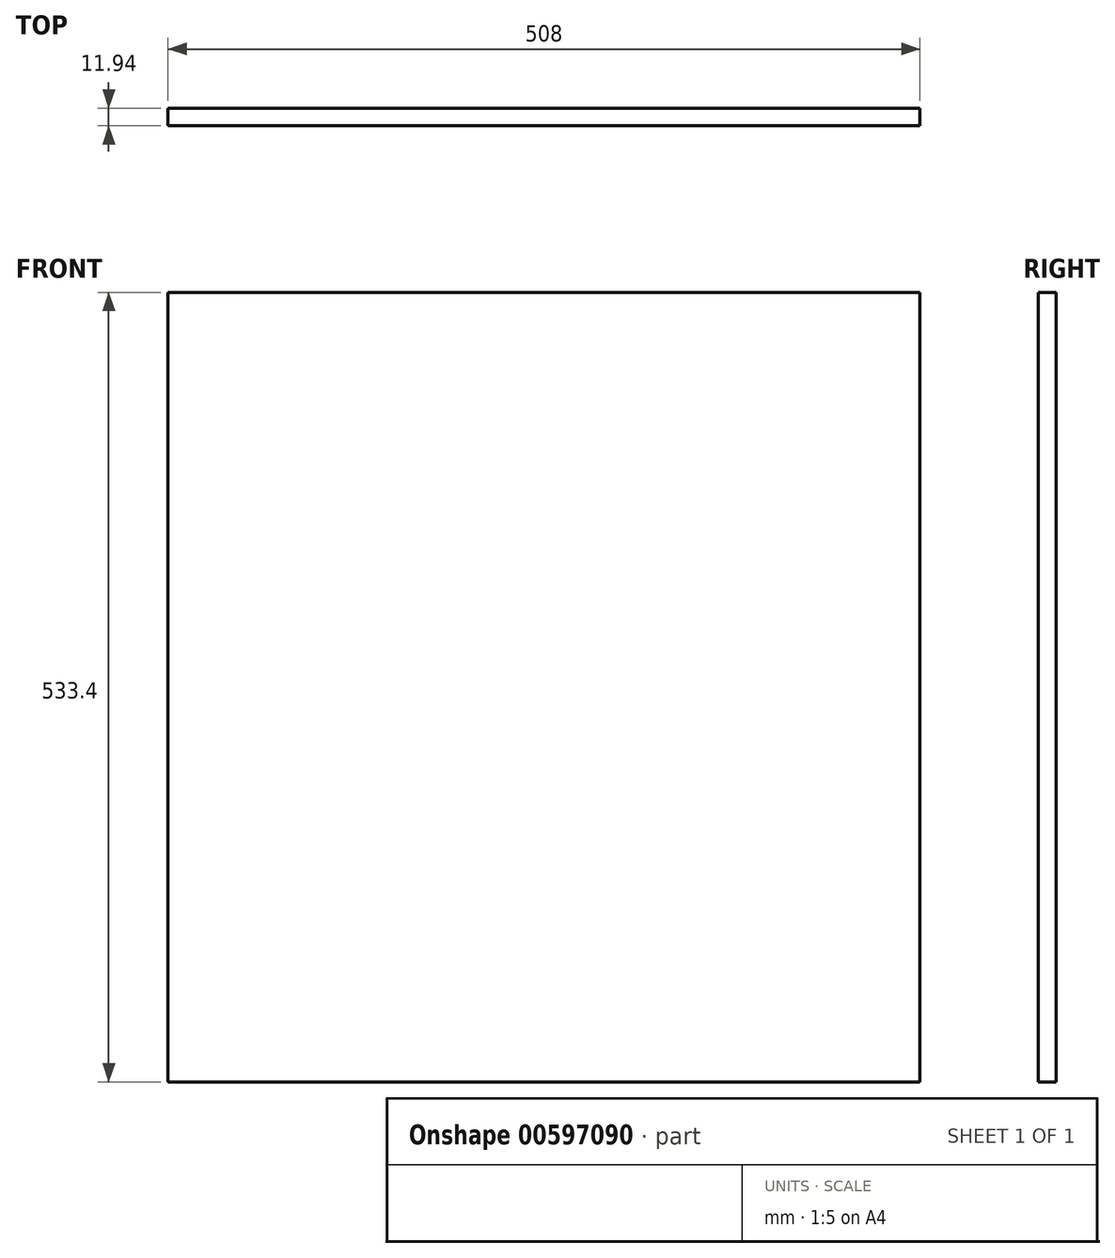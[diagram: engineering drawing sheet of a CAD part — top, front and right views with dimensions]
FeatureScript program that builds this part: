
annotation { "Feature Type Name" : "Feature", "Feature Type Description" : "" }
export const myFeature = defineFeature(function(context is Context, id is Id, definition is map)
    precondition{}
    {
        {
            var Q0;
            Q0=qCreatedBy(makeId("Front.planeOp"),FACE);
            var sketch = newSketch(context, id + "F0", { "sketchPlane" : qUnion([Q0])});
            skLineSegment(sketch, "E0.bottom", {"start": v(-240.33, 326.42) * mm, "end": v(267.67, 326.42) * mm});
            skLineSegment(sketch, "E0.top", {"start": v(-240.33, -206.98) * mm, "end": v(267.67, -206.98) * mm});
            skLineSegment(sketch, "E0.left", {"start": v(-240.33, 326.42) * mm, "end": v(-240.33, -206.98) * mm});
            skLineSegment(sketch, "E0.right", {"start": v(267.67, 326.42) * mm, "end": v(267.67, -206.98) * mm});
            skSolve(sketch);
        }
        {
            var Q0;
            Q0 = qSketchRegion(id + "F0", true);
            extrude(context, id + "F1", {"entities" : qUnion([Q0]), "depth" : 11.94 * mm, "offsetDistance" : 25.4 * mm});
        }
    });
